# Revit family: HP-Bearing Pile
name_source: partatom
category: Structural Framing
revit_build: Autodesk Revit Architecture 2012 (Build: 20110210_1515)
units: mm (PartAtom-declared; Revit-internal decimal feet)

## types (11) — shared parameters
Assembly Code = B10

## per-type parameters (varying)
| type | A | W | bf | d | k | k2 | tf | tw |
| HP14X117 | 34.4 in² | 117 | 1' - 2 7/8" | 1' - 2 3/16" | 0' - 1 1/2" | 0' - 0 11/16" | 0' - 0 13/16" | 0' - 0 13/16" |
| HP14X102 | 30 in² | 102 | 1' - 2 13/16" | 1' - 2" | 0' - 1 3/8" | 0' - 0 11/16" | 0' - 0 11/16" | 0' - 0 11/16" |
| HP14X89 | 26.1 in² | 89 | 1' - 2 11/16" | 1' - 1 13/16" | 0' - 1 5/16" | 0' - 0 11/16" | 0' - 0 5/8" | 0' - 0 5/8" |
| HP14X73 | 21.4 in² | 73 | 1' - 2 5/8" | 1' - 1 5/8" | 0' - 1 3/16" | 0' - 0 11/16" | 0' - 0 1/2" | 0' - 0 1/2" |
| HP12X84 | 24.6 in² | 84 | 1' - 0 5/16" | 1' - 0 5/16" | 0' - 1 3/8" | 0' - 0 11/16" | 0' - 0 11/16" | 0' - 0 11/16" |
| HP12X74 | 21.8 in² | 74 | 1' - 0 3/16" | 1' - 0 1/8" | 0' - 1 5/16" | 0' - 0 11/16" | 0' - 0 5/8" | 0' - 0 5/8" |
| HP12X63 | 18.4 in² | 63 | 1' - 0 1/8" | 0' - 11 7/8" | 0' - 1 1/4" | 0' - 0 3/4" | 0' - 0 1/2" | 0' - 0 1/2" |
| HP12X53 | 15.5 in² | 53 | 1' - 0" | 0' - 11 13/16" | 0' - 1 1/8" | 0' - 0 11/16" | 0' - 0 7/16" | 0' - 0 7/16" |
| HP10X57 | 16.8 in² | 57 | 0' - 10 3/16" | 0' - 10" | 0' - 1 1/4" | 0' - 0 11/16" | 0' - 0 9/16" | 0' - 0 9/16" |
| HP10X42 | 12.4 in² | 42 | 0' - 10 1/8" | 0' - 9 11/16" | 0' - 1 1/8" | 0' - 0 11/16" | 0' - 0 7/16" | 0' - 0 7/16" |
| HP8X36 | 10.6 in² | 36 | 0' - 8 3/16" | 0' - 8" | 0' - 1 1/8" | 0' - 0 11/16" | 0' - 0 7/16" | 0' - 0 7/16" |

## geometry (parser evidence)
native form markers: Sweep x1
no freeform markers — native parametric forms only
